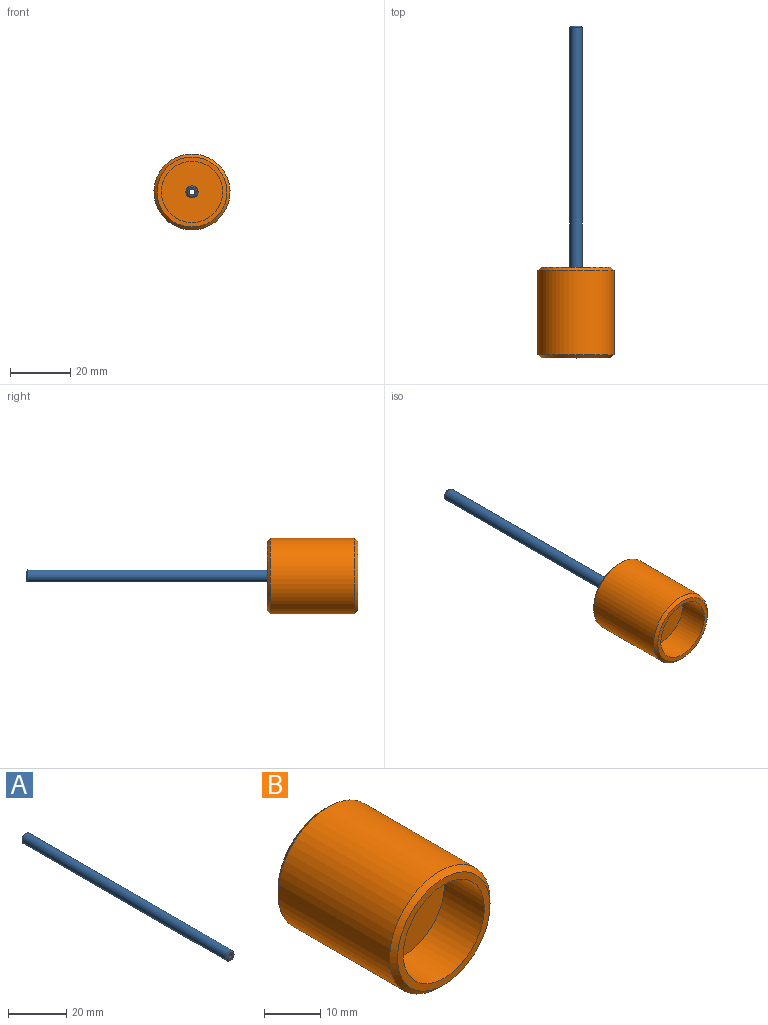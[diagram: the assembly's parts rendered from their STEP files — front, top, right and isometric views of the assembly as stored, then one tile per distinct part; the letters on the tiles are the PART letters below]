
ASSEMBLY  parts=2 mates=1
PART A: 6 faces, bbox 4x100x4 mm
  f0: cylinder r=1mm len=100mm, axis (0,1,0), area 628.3mm2, adj f2,f3
  f1: cylinder r=2mm len=99mm, axis (0,1,0), area 1244.1mm2, adj f4,f5
  f2: plane 3x3mm, normal (0,-1,0), area 3.9mm2, adj f0,f5
  f3: plane 3x3mm, normal (0,1,0), area 3.9mm2, adj f0,f4
  f4: cone r=2mm half-angle=45deg, axis (0,-1,0), area 7.8mm2, adj f1,f3
  f5: cone r=1.5mm half-angle=45deg, axis (0,1,0), area 7.8mm2, adj f1,f2
PART B: 9 faces, bbox 25.2x30x25.2 mm
  f0: cylinder r=12.6mm len=28mm, axis (0,1,0), area 2216.7mm2, adj f6,f7
  f1: plane 23.2x23.2mm, normal (0,-1,0), area 98.4mm2, adj f3,f6
  f2: plane 23.2x23.2mm, normal (0,1,0), area 403.1mm2, adj f7,f8
  f3: cylinder r=10.16mm len=20.32mm, axis (0,-1,0), area 638.4mm2, adj f1,f4
  f4: plane 20.32x20.32mm, normal (0,-1,0), area 311.8mm2, adj f3,f5
  f5: cylinder r=2mm len=19.5mm, axis (0,1,0), area 245mm2, adj f4,f8
  f6: cone r=11.6mm half-angle=45deg, axis (0,1,0), area 107.5mm2, adj f0,f1
  f7: cone r=12.6mm half-angle=45deg, axis (0,-1,0), area 107.5mm2, adj f0,f2
  f8: cone r=2mm half-angle=45deg, axis (0,1,0), area 10mm2, adj f2,f5
PLACE A t=(-59.67,85.28,-44.46)mm
PLACE B t=(-11.84,5.28,-4.32)mm
MATE parallel A.f0 <-> B.f5  axis (0,-1,0) through (-11.84,-14.72,-4.32)mm
